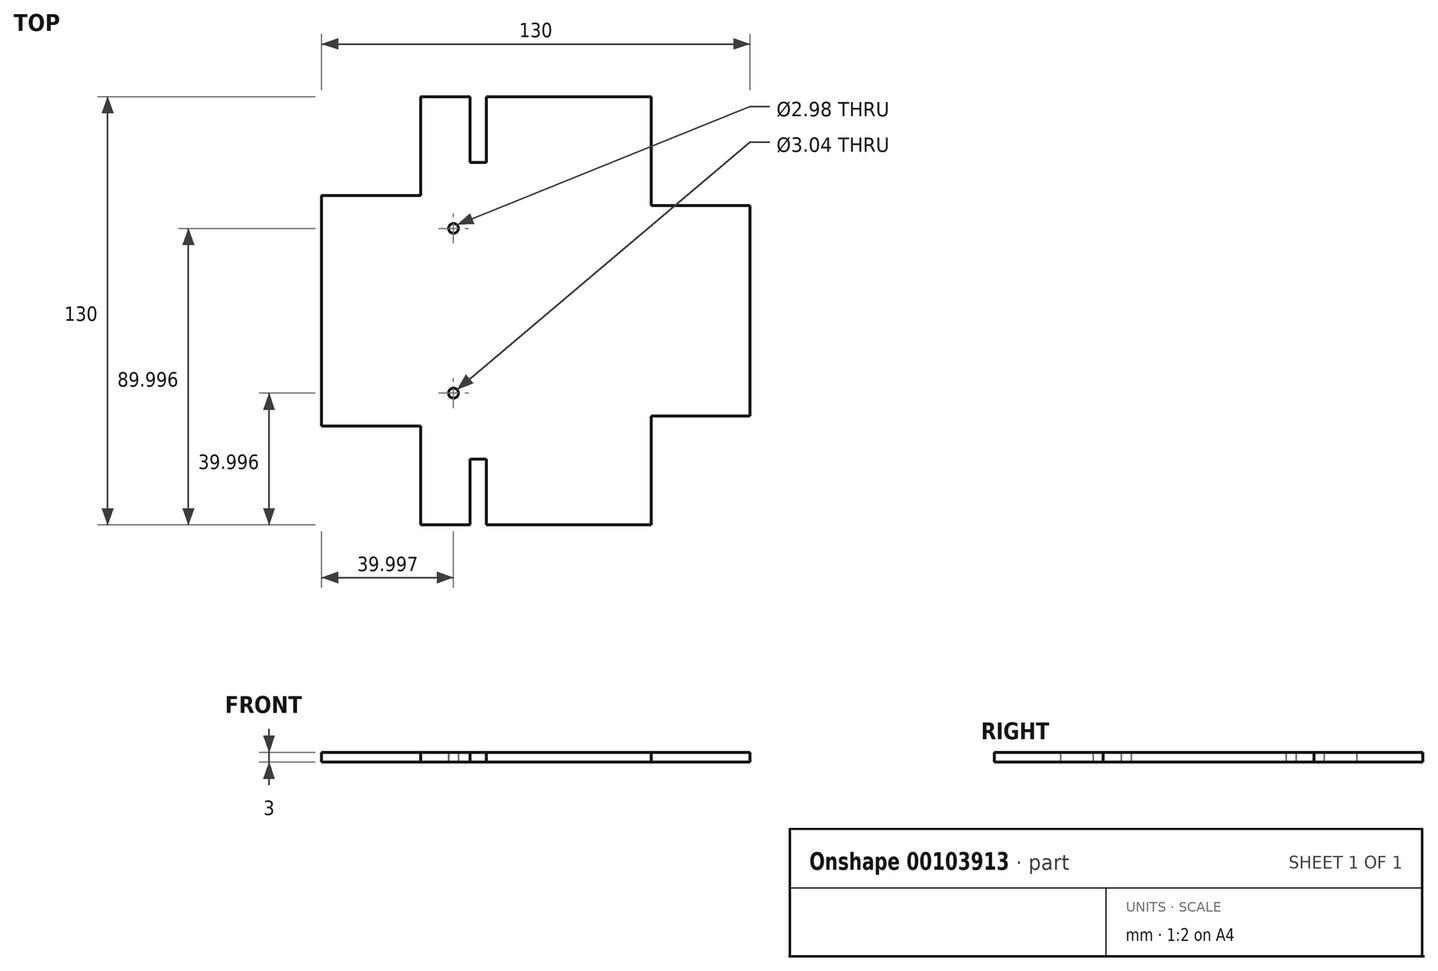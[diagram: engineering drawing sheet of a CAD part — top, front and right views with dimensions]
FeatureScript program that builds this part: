
annotation { "Feature Type Name" : "Feature", "Feature Type Description" : "" }
export const myFeature = defineFeature(function(context is Context, id is Id, definition is map)
    precondition{}
    {
        {
            var Q0;
            Q0=qCreatedBy(makeId("Top.planeOp"),FACE);
            var sketch = newSketch(context, id + "F0", { "sketchPlane" : qUnion([Q0])});
            skLineSegment(sketch, "E0.bottom", {"start": v(-54.97, 87.47) * mm, "end": v(-39.97, 87.47) * mm});
            skLineSegment(sketch, "E0.top", {"start": v(-54.97, -42.53) * mm, "end": v(-39.97, -42.53) * mm});
            skLineSegment(sketch, "E0.right", {"start": v(45.03, 54.47) * mm, "end": v(45.03, -9.53) * mm});
            skLineSegment(sketch, "E1.top", {"start": v(-84.97, 57.47) * mm, "end": v(-54.97, 57.47) * mm});
            skLineSegment(sketch, "E1.right", {"start": v(-54.97, 87.47) * mm, "end": v(-54.97, 57.47) * mm});
            skLineSegment(sketch, "E2.bottom", {"start": v(-84.97, -12.53) * mm, "end": v(-54.97, -12.53) * mm});
            skLineSegment(sketch, "E2.right", {"start": v(-54.97, -12.53) * mm, "end": v(-54.97, -42.53) * mm});
            skLineSegment(sketch, "E3.top", {"start": v(15.03, 54.47) * mm, "end": v(45.03, 54.47) * mm});
            skLineSegment(sketch, "E3.left", {"start": v(15.03, 87.47) * mm, "end": v(15.03, 54.47) * mm});
            skLineSegment(sketch, "E4.top", {"start": v(15.03, -9.53) * mm, "end": v(45.03, -9.53) * mm});
            skLineSegment(sketch, "E4.left", {"start": v(15.03, -42.53) * mm, "end": v(15.03, -9.53) * mm});
            skLineSegment(sketch, "E5.top", {"start": v(-39.97, 67.47) * mm, "end": v(-34.97, 67.47) * mm});
            skLineSegment(sketch, "E5.left", {"start": v(-39.97, 87.47) * mm, "end": v(-39.97, 67.47) * mm});
            skLineSegment(sketch, "E5.right", {"start": v(-34.97, 87.47) * mm, "end": v(-34.97, 67.47) * mm});
            skLineSegment(sketch, "E6.top", {"start": v(-39.97, -22.53) * mm, "end": v(-34.97, -22.53) * mm});
            skLineSegment(sketch, "E6.left", {"start": v(-39.97, -42.53) * mm, "end": v(-39.97, -22.53) * mm});
            skLineSegment(sketch, "E6.right", {"start": v(-34.97, -42.53) * mm, "end": v(-34.97, -22.53) * mm});
            skPoint(sketch, "E7.orphan", {"position": v(-84.97, -42.53) * mm});
            skLineSegment(sketch, "E8.trimOffspring", {"start": v(-34.97, -42.53) * mm, "end": v(15.03, -42.53) * mm});
            skPoint(sketch, "E9.orphan", {"position": v(45.03, 87.47) * mm});
            skPoint(sketch, "E10.orphan", {"position": v(-84.97, 87.47) * mm});
            skLineSegment(sketch, "E11", {"start": v(-84.97, 57.47) * mm, "end": v(-84.97, -12.53) * mm});
            skLineSegment(sketch, "E12.trimOffspring", {"start": v(-34.97, 87.47) * mm, "end": v(15.03, 87.47) * mm});
            skCircle(sketch, "E13", {"center": v(-44.97, 47.47) * mm, "radius": 1.49 * mm});
            skCircle(sketch, "E14", {"center": v(-44.97, -2.53) * mm, "radius": 1.52 * mm});
            skSolve(sketch);
        }
        {
            var Q0;
            Q0 = qSketchRegion(id + "F0", true);
            extrude(context, id + "F1", {"entities" : qUnion([Q0]), "depth" : 3 * mm});
        }
    });
